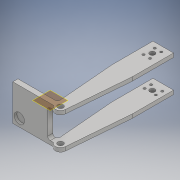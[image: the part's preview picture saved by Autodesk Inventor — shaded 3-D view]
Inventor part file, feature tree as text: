
AUTODESK INVENTOR PART (.ipt)
format: ipt  version: 2017 (Build 210142000, 142)  size: 245,248 bytes
history: native  units: in
note: dims shown in document units (in); Inventor stores cm internally (conversion verified against a paired STEP export)
features: sketch x9, projected_geometry x9, hole x5, extrude x4, plane x2, fillet x2
ambient origin geometry x8: Origin, YZ Plane, XZ Plane, XY Plane, X Axis, Y Axis, Z Axis, Center Point
bodies: Solid1 (feature_tree)
feature tree (31):
  sketch  "Sketch1"  dims[d0=5.0in d1=1.0in]
  plane  "Work Plane1"
  extrude  "Extrusion2"  Depth=1.0in
  plane  "Work Plane2"
  extrude  "Extrusion3"  Depth=0.5in
  hole  "Hole2"  [1 undecoded]
  extrude  "Extrusion4"  Depth=0.5in
  extrude  "Extrusion5"  Depth=1.753in
  fillet  "Fillet1"  Radius=2.0in
  fillet  "Fillet2"  Radius=1.753in
  hole  "Hole3"  [1 undecoded]
  hole  "Hole4"  [1 undecoded]
  hole  "Hole5"  [1 undecoded]
  hole  "Hole6"  [1 undecoded]
  sketch  "Sketch2"  dims[d5=1.0in d6=0.5in]
  projected_geometry  "Projected Loop1"
  sketch  "Sketch4"  dims[d7=0.5in d8=0.0in]
  projected_geometry  "Projected Loop3"
  sketch  "Sketch5"  dims[d9=1.753in d10=0.0in d18=0.5in]
  projected_geometry  "Projected Loop4"
  sketch  "Sketch8"  dims[d19=0.25in d20=2.0in d21=2.0in d22=1.753in d23=0.0in]
  projected_geometry  "Projected Loop9"
  projected_geometry  "Projected Loop10"
  sketch  "Sketch9"  dims[d24=0.27in d25=0.75in d26=0.375in d27=0.25in d28=0.5635in d29=1.0in d30=0.8108in d31=2.0in]
  projected_geometry  "Projected Loop11"
  sketch  "Sketch10"  dims[d32=0.25in d35=5.0in]
  projected_geometry  "Projected Loop12"
  sketch  "Sketch11"  dims[d36=4.875in d37=1.753in d38=0.0in]
  projected_geometry  "Projected Loop13"
  sketch  "Sketch12"  dims[d41=1.753in d42=5.375in d43=1.378in d44=0.1875in d45=5.875in d46=1.0in d47=0.0in d48=0.125in d49=0.125in d50=0.6299in d51=1.0in d52=0.5in d53=0.315in d54=0.1575in d55=0.117in d56=0.75in d57=0.375in d58=0.25in d59=0.5635in d60=1.0in d61=0.8108in d62=0.6299in d63=1.0in d64=0.5in d65=0.315in d66=0.1575in d67=0.117in d68=0.75in d69=0.375in d70=0.25in d71=0.5635in d72=1.0in d73=0.8108in d74=0.32in d75=1.753in d77=0.5in d78=0.75in d79=0.375in d80=0.25in d81=0.5635in d82=0.125in d83=0.0in d84=1.0in d85=0.5in d86=0.5455in d87=0.2728in d88=0.25in d89=0.75in d90=0.375in d91=0.25in d92=0.5635in d93=1.0in d94=0.8108in d95=0.27in d96=0.1975in d97=0.375in]
  projected_geometry  "Projected Loop14"
note: 5 required parameter values undecoded (feature->parameter linkage not recoverable at this tier; creation-order binding heuristic only, values carry confidence <= 0.55)
